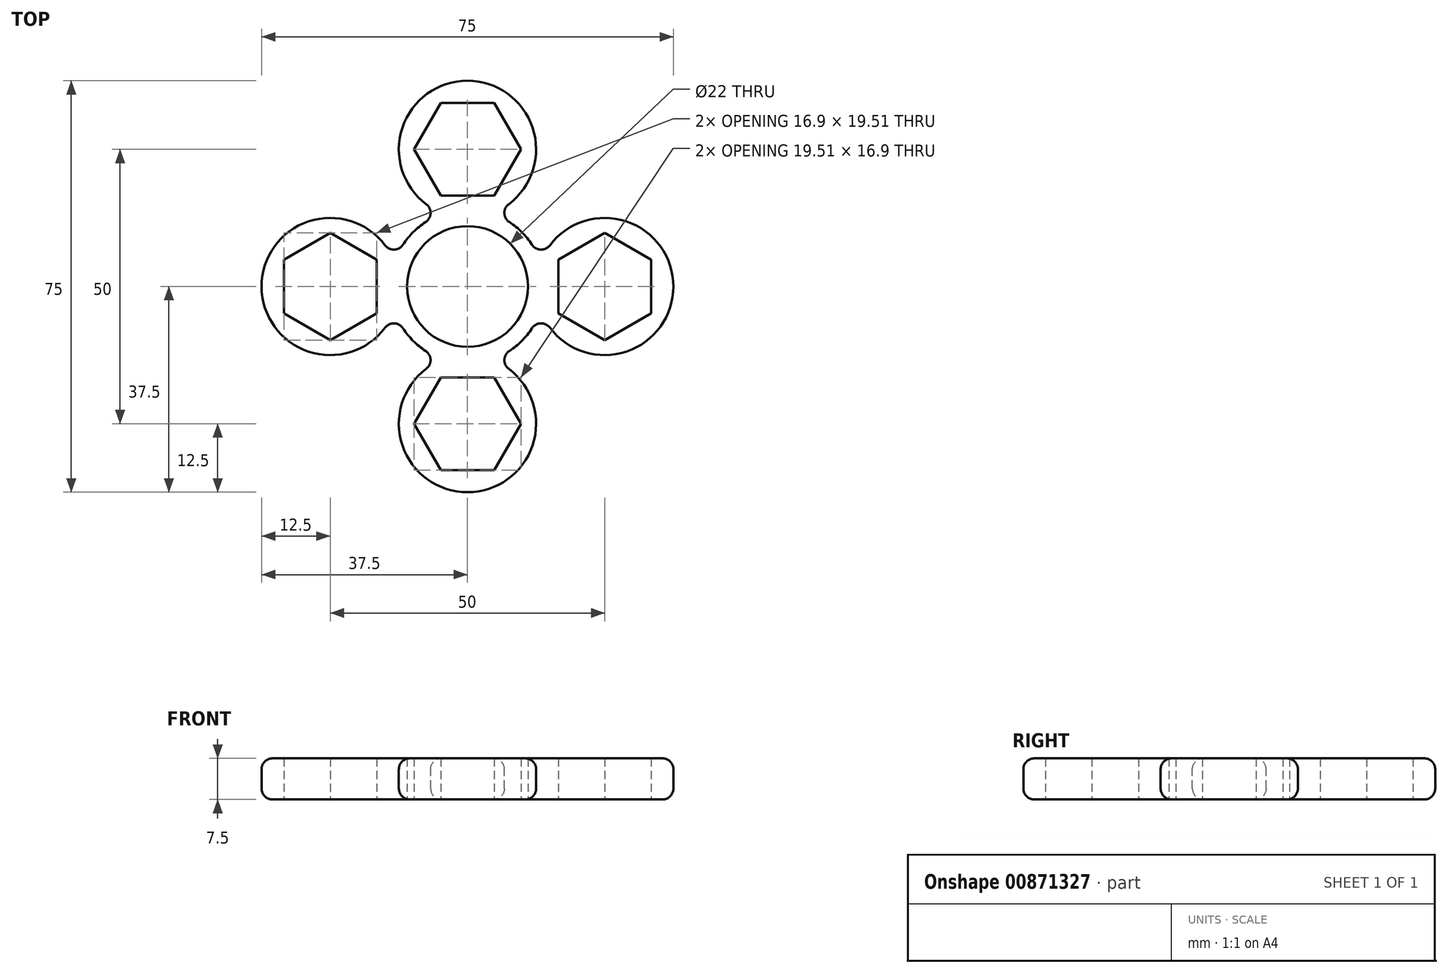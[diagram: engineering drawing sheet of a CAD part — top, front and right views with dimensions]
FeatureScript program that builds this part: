
annotation { "Feature Type Name" : "Feature", "Feature Type Description" : "" }
export const myFeature = defineFeature(function(context is Context, id is Id, definition is map)
    precondition{}
    {
        {
            var Q0;
            Q0=qCreatedBy(makeId("Top.planeOp"),FACE);
            var sketch = newSketch(context, id + "F0", { "sketchPlane" : qUnion([Q0])});
            skArc(sketch, "E0", {"start": v(-13.3, -4.39) * mm, "mid": v(-9.9, -9.9) * mm, "end": v(-4.39, -13.3) * mm});
            skCircle(sketch, "E1", {"center": v(0, 0) * mm, "radius": 11 * mm});
            skCircle(sketch, "E2.cCircle", {"center": v(-25, 0) * mm, "radius": 8.45 * mm, "construction": true});
            skLineSegment(sketch, "E2.0", {"start": v(-16.55, 4.88) * mm, "end": v(-16.55, -4.88) * mm});
            skLineSegment(sketch, "E2.1", {"start": v(-16.55, -4.88) * mm, "end": v(-25, -9.76) * mm});
            skLineSegment(sketch, "E2.2", {"start": v(-25, -9.76) * mm, "end": v(-33.45, -4.88) * mm});
            skLineSegment(sketch, "E2.3", {"start": v(-33.45, -4.88) * mm, "end": v(-33.45, 4.88) * mm});
            skLineSegment(sketch, "E2.4", {"start": v(-33.45, 4.88) * mm, "end": v(-25, 9.76) * mm});
            skLineSegment(sketch, "E2.5", {"start": v(-25, 9.76) * mm, "end": v(-16.55, 4.88) * mm});
            skPoint(sketch, "E2.0.midPoint", {"position": v(-16.55, 0) * mm});
            skLineSegment(sketch, "E3.MirrorCS", {"start": v(25, 9.76) * mm, "end": v(16.55, 4.88) * mm});
            skLineSegment(sketch, "E4.MirrorCS", {"start": v(33.45, 4.88) * mm, "end": v(25, 9.76) * mm});
            skLineSegment(sketch, "E5.MirrorCS", {"start": v(33.45, -4.88) * mm, "end": v(33.45, 4.88) * mm});
            skLineSegment(sketch, "E6.MirrorCS", {"start": v(25, -9.76) * mm, "end": v(33.45, -4.88) * mm});
            skLineSegment(sketch, "E7.MirrorCS", {"start": v(16.55, -4.88) * mm, "end": v(25, -9.76) * mm});
            skLineSegment(sketch, "E8.MirrorCS", {"start": v(16.55, 4.88) * mm, "end": v(16.55, -4.88) * mm});
            skArc(sketch, "E9", {"start": v(-13.3, 4.39) * mm, "mid": v(-37.5, 0) * mm, "end": v(-13.3, -4.39) * mm});
            skArc(sketch, "E10.MirrorCS", {"start": v(13.3, 4.39) * mm, "mid": v(37.5, 0) * mm, "end": v(13.3, -4.39) * mm});
            skArc(sketch, "E11.trimOffspring", {"start": v(13.3, 4.39) * mm, "mid": v(9.9, 9.9) * mm, "end": v(4.39, 13.3) * mm});
            skArc(sketch, "E12", {"start": v(4.39, 13.3) * mm, "mid": v(0, 37.5) * mm, "end": v(-4.39, 13.3) * mm});
            skArc(sketch, "E13.trimOffspring", {"start": v(-4.39, 13.3) * mm, "mid": v(-9.9, 9.9) * mm, "end": v(-13.3, 4.39) * mm});
            skCircle(sketch, "E14.cCircle", {"center": v(0, 25) * mm, "radius": 8.45 * mm, "construction": true});
            skLineSegment(sketch, "E14.0", {"start": v(-4.88, 33.45) * mm, "end": v(4.88, 33.45) * mm});
            skLineSegment(sketch, "E14.1", {"start": v(4.88, 33.45) * mm, "end": v(9.76, 25) * mm});
            skLineSegment(sketch, "E14.2", {"start": v(9.76, 25) * mm, "end": v(4.88, 16.55) * mm});
            skLineSegment(sketch, "E14.3", {"start": v(4.88, 16.55) * mm, "end": v(-4.88, 16.55) * mm});
            skLineSegment(sketch, "E14.4", {"start": v(-4.88, 16.55) * mm, "end": v(-9.76, 25) * mm});
            skLineSegment(sketch, "E14.5", {"start": v(-9.76, 25) * mm, "end": v(-4.88, 33.45) * mm});
            skPoint(sketch, "E14.0.midPoint", {"position": v(0, 33.45) * mm});
            skArc(sketch, "E15.MirrorCS", {"start": v(4.39, -13.3) * mm, "mid": v(0, -37.5) * mm, "end": v(-4.39, -13.3) * mm});
            skLineSegment(sketch, "E16.MirrorCS", {"start": v(-4.88, -16.55) * mm, "end": v(-9.76, -25) * mm});
            skLineSegment(sketch, "E17.MirrorCS", {"start": v(-9.76, -25) * mm, "end": v(-4.88, -33.45) * mm});
            skLineSegment(sketch, "E18.MirrorCS", {"start": v(-4.88, -33.45) * mm, "end": v(4.88, -33.45) * mm});
            skLineSegment(sketch, "E19.MirrorCS", {"start": v(4.88, -33.45) * mm, "end": v(9.76, -25) * mm});
            skLineSegment(sketch, "E20.MirrorCS", {"start": v(9.76, -25) * mm, "end": v(4.88, -16.55) * mm});
            skLineSegment(sketch, "E21.MirrorCS", {"start": v(4.88, -16.55) * mm, "end": v(-4.88, -16.55) * mm});
            skArc(sketch, "E22.trimOffspring", {"start": v(4.39, -13.3) * mm, "mid": v(9.9, -9.9) * mm, "end": v(13.3, -4.39) * mm});
            skSolve(sketch);
        }
        {
            var Q0;
            Q0=makeQuery(id+"F0.imprint","IMPRINT",FACE,{"disambiguationData":[TD([[makeQuery(id+"F0.imprint","IMPRINT",EDGE,{"derivedFrom":sQuery(id+"F0.wireOp",EDGE,"E0")}),1.0]])]});
            extrude(context, id + "F1", {"entities" : qUnion([Q0]), "depth" : 7.5 * mm, "offsetDistance" : 25 * mm});
        }
        {
            var Q0;
            Q0=makeQuery(id+"F1.opExtrude","SWEPT_EDGE",EDGE,{"disambiguationData":[OSD([sQuery(id+"F0.wireOp",EDGE,"E0"),sQuery(id+"F0.wireOp",EDGE,"E9")])]});
            var Q1;
            Q1=makeQuery(id+"F1.opExtrude","SWEPT_EDGE",EDGE,{"disambiguationData":[OSD([sQuery(id+"F0.wireOp",EDGE,"E0"),sQuery(id+"F0.wireOp",EDGE,"E10.MirrorCS")])]});
            var Q2;
            Q2=makeQuery(id+"F1.opExtrude","SWEPT_EDGE",EDGE,{"disambiguationData":[OSD([sQuery(id+"F0.wireOp",EDGE,"E10.MirrorCS"),sQuery(id+"F0.wireOp",EDGE,"E11.trimOffspring")])]});
            var Q3;
            Q3=makeQuery(id+"F1.opExtrude","SWEPT_EDGE",EDGE,{"disambiguationData":[OSD([sQuery(id+"F0.wireOp",EDGE,"E9"),sQuery(id+"F0.wireOp",EDGE,"E11.trimOffspring")])]});
            var Q4;
            Q4=makeQuery(id+"F1.opExtrude","SWEPT_EDGE",EDGE,{"disambiguationData":[OSD([sQuery(id+"F0.wireOp",EDGE,"E15.MirrorCS"),sQuery(id+"F0.wireOp",EDGE,"E22.trimOffspring")])]});
            var Q5;
            Q5=makeQuery(id+"F1.opExtrude","SWEPT_EDGE",EDGE,{"disambiguationData":[OSD([sQuery(id+"F0.wireOp",EDGE,"E12"),sQuery(id+"F0.wireOp",EDGE,"E13.trimOffspring")])]});
            fillet(context, id + "F2", {"entities" : qUnion([Q0, Q1, Q2, Q3, Q4, Q5]), "radius" : 2 * mm, "tangentPropagation" : true, "allowEdgeOverflow" : false});
        }
        {
            var Q0;
            Q0=makeQuery(id+"F1.opExtrude","CAP_EDGE",EDGE,{"disambiguationData":[OSD([sQuery(id+"F0.wireOp",EDGE,"E9")])],"isStart":false});
            var Q1;
            Q1=makeQuery(id+"F1.opExtrude","CAP_EDGE",EDGE,{"disambiguationData":[OSD([sQuery(id+"F0.wireOp",EDGE,"E9")])],"isStart":true});
            fillet(context, id + "F3", {"entities" : qUnion([Q0, Q1]), "radius" : 2 * mm, "tangentPropagation" : true, "allowEdgeOverflow" : false});
        }
    });
